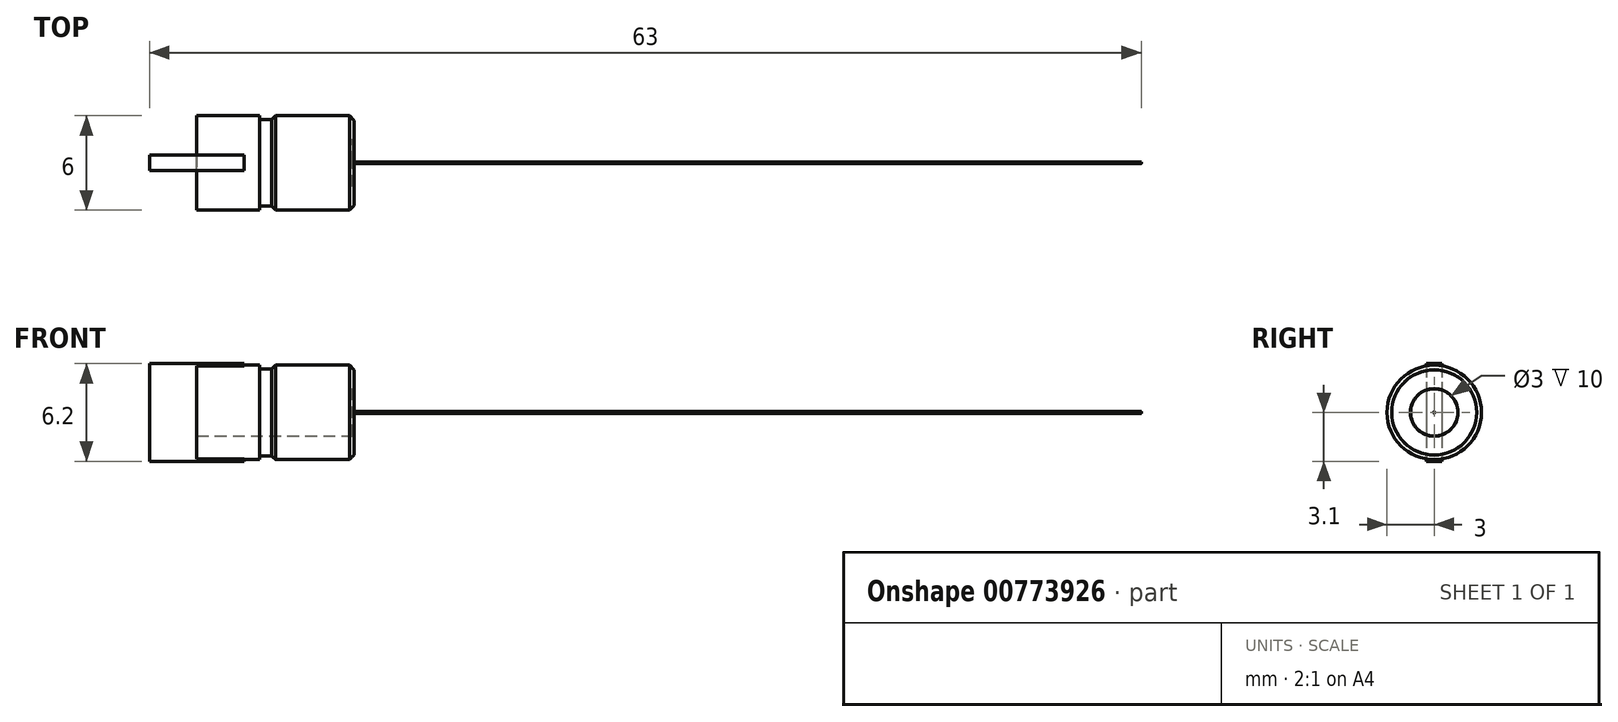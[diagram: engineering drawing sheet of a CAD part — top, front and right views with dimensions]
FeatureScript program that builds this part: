
annotation { "Feature Type Name" : "Feature", "Feature Type Description" : "" }
export const myFeature = defineFeature(function(context is Context, id is Id, definition is map)
    precondition{}
    {
        {
            var Q0;
            Q0=qCreatedBy(makeId("Right.planeOp"),FACE);
            var sketch = newSketch(context, id + "F0", { "sketchPlane" : qUnion([Q0])});
            skCircle(sketch, "E0", {"center": v(0, 0) * mm, "radius": 3 * mm});
            skSolve(sketch);
        }
        {
            var Q0;
            Q0 = qSketchRegion(id + "F0", true);
            extrude(context, id + "F1", {"entities" : qUnion([Q0]), "depth" : 5 * mm, "offsetDistance" : 25 * mm});
        }
        {
            var Q0;
            Q0=makeQuery(id+"F1.opExtrude","CAP_FACE",FACE,{"disambiguationData":[OSD([sQuery(id+"F0.wireOp",EDGE,"E0")])],"isStart":true});
            var sketch = newSketch(context, id + "F2", { "sketchPlane" : qUnion([Q0])});
            skCircle(sketch, "E1", {"center": v(0, 0) * mm, "radius": 2.75 * mm});
            skSolve(sketch);
        }
        {
            var Q0;
            Q0 = qSketchRegion(id + "F2", true);
            extrude(context, id + "F3", {"entities" : qUnion([Q0]), "operationType" : NewBodyOperationType.ADD, "depth" : 1 * mm, "offsetDistance" : 25 * mm});
        }
        {
            var Q0;
            Q0=makeQuery(id+"F3.opExtrude","CAP_FACE",FACE,{"disambiguationData":[OSD([sQuery(id+"F2.wireOp",EDGE,"E1")])],"isStart":false});
            var sketch = newSketch(context, id + "F4", { "sketchPlane" : qUnion([Q0])});
            skCircle(sketch, "E2", {"center": v(0, 0) * mm, "radius": 3 * mm});
            skSolve(sketch);
        }
        {
            var Q0;
            Q0 = qSketchRegion(id + "F4", true);
            extrude(context, id + "F5", {"entities" : qUnion([Q0]), "operationType" : NewBodyOperationType.ADD, "depth" : 4 * mm, "offsetDistance" : 25 * mm});
        }
        {
            var Q0;
            Q0=makeQuery(id+"F5.opExtrude","CAP_FACE",FACE,{"disambiguationData":[OSD([sQuery(id+"F4.wireOp",EDGE,"E2")])],"isStart":false});
            var sketch = newSketch(context, id + "F6", { "sketchPlane" : qUnion([Q0])});
            skLineSegment(sketch, "E3.bottom", {"start": v(-0.5, 3.1) * mm, "end": v(0.5, 3.1) * mm});
            skLineSegment(sketch, "E3.top", {"start": v(-0.5, -3.1) * mm, "end": v(0.5, -3.1) * mm});
            skLineSegment(sketch, "E3.left", {"start": v(-0.5, 3.1) * mm, "end": v(-0.5, -3.1) * mm});
            skLineSegment(sketch, "E3.right", {"start": v(0.5, 3.1) * mm, "end": v(0.5, -3.1) * mm});
            skSolve(sketch);
        }
        {
            var Q0;
            Q0 = qSketchRegion(id + "F6", true);
            extrude(context, id + "F7", {"entities" : qUnion([Q0]), "operationType" : NewBodyOperationType.ADD, "depth" : 3 * mm, "offsetDistance" : 25 * mm});
        }
        {
            var Q0;
            Q0 = qSketchRegion(id + "F6", true);
            extrude(context, id + "F8", {"entities" : qUnion([Q0]), "operationType" : NewBodyOperationType.ADD, "oppositeDirection" : true, "depth" : 3 * mm, "offsetDistance" : 25 * mm});
        }
        {
            var Q0;
            Q0 = qSketchRegion(id + "F0", true);
            extrude(context, id + "F9", {"entities" : qUnion([Q0]), "operationType" : NewBodyOperationType.ADD, "oppositeDirection" : true, "depth" : 0.5 * mm, "offsetDistance" : 25 * mm});
        }
        {
            var Q0;
            Q0=makeQuery(id+"F9.opExtrude","CAP_EDGE",EDGE,{"disambiguationData":[OSD([sQuery(id+"F0.wireOp",EDGE,"E0")])],"isStart":false});
            chamfer(context, id + "F10", {"entities" : qUnion([Q0]), "width" : 0.5 * mm, "tangentPropagation" : true});
        }
        {
            var Q0;
            Q0=makeQuery(id+"F1.opExtrude","CAP_EDGE",EDGE,{"disambiguationData":[OSD([sQuery(id+"F0.wireOp",EDGE,"E0")])],"isStart":false});
            chamfer(context, id + "F11", {"entities" : qUnion([Q0]), "width" : 0.3 * mm, "tangentPropagation" : true});
        }
        {
            var Q0;
            Q0=makeQuery(id+"F1.opExtrude","CAP_FACE",FACE,{"disambiguationData":[OSD([sQuery(id+"F0.wireOp",EDGE,"E0")])],"isStart":false});
            var sketch = newSketch(context, id + "F12", { "sketchPlane" : qUnion([Q0])});
            skCircle(sketch, "E4", {"center": v(0, 0) * mm, "radius": 1.5 * mm});
            skSolve(sketch);
        }
        {
            var Q0;
            Q0 = qSketchRegion(id + "F12", true);
            extrude(context, id + "F13", {"entities" : qUnion([Q0]), "operationType" : NewBodyOperationType.REMOVE, "oppositeDirection" : true, "depth" : 10 * mm, "offsetDistance" : 25 * mm});
        }
        {
            var Q0;
            Q0=makeQuery(id+"F1.opExtrude","CAP_FACE",FACE,{"disambiguationData":[OSD([sQuery(id+"F0.wireOp",EDGE,"E0")])],"isStart":false});
            var sketch = newSketch(context, id + "F14", { "sketchPlane" : qUnion([Q0])});
            skCircle(sketch, "E5", {"center": v(0, 0) * mm, "radius": 0.05 * mm});
            skSolve(sketch);
        }
        {
            var Q0;
            Q0 = qSketchRegion(id + "F14", true);
            extrude(context, id + "F15", {"entities" : qUnion([Q0]), "depth" : 50 * mm, "offsetDistance" : 25 * mm});
        }
        {
            var Q0;
            Q0=makeQuery(id+"F1.opExtrude","CAP_FACE",FACE,{"disambiguationData":[OSD([sQuery(id+"F0.wireOp",EDGE,"E0")])],"isStart":false});
            var sketch = newSketch(context, id + "F16", { "sketchPlane" : qUnion([Q0])});
            skCircle(sketch, "E6", {"center": v(0, 0) * mm, "radius": 1.51 * mm});
            skSolve(sketch);
        }
        {
            var Q0;
            Q0 = qSketchRegion(id + "F16", true);
            extrude(context, id + "F17", {"entities" : qUnion([Q0]), "oppositeDirection" : true, "depth" : 0.1 * mm, "offsetDistance" : 25 * mm});
        }
    });
